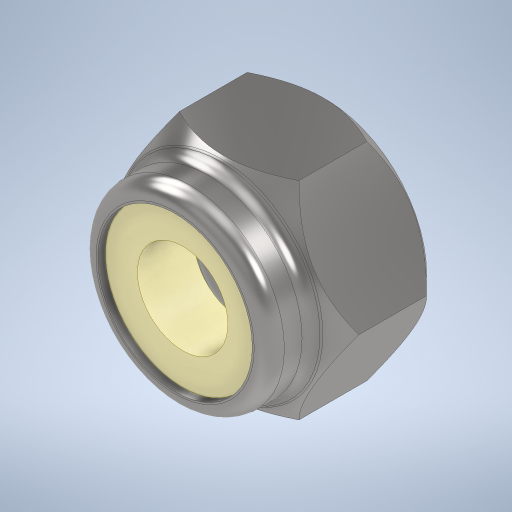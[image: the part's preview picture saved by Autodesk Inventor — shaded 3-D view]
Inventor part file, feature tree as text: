
AUTODESK INVENTOR PART (.ipt)
format: ipt  version: 2024 (Build 280153000, 153)  size: 372,224 bytes
history: native  units: mm
features: sketch x6, extrude x5, chamfer x2, hole x2, fillet x1, projected_geometry x1, other x1
ambient origin geometry x8: Origin, YZ Plane, XZ Plane, XY Plane, X Axis, Y Axis, Z Axis, Center Point
bodies: Solid1 (feature_tree)
feature tree (18):
  sketch  "Sketch1"  dims[d0=5.5mm d2=2.8mm d3=0.0mm d4=0.5mm d5=2.0mm d6=45.0deg]
  extrude  "Extrusion1"  Depth=2.8mm TaperAngle=0.0deg
  chamfer  "Chamfer1"  Distance=0.5mm Angle=45.0deg
  extrude  "Extrusion2"  Depth=5.0mm
  extrude  "Extrusion3"  Depth=0.4mm
  fillet  "Fillet1"  Radius=4.1mm
  extrude  "Extrusion4"  Depth=1.5mm TaperAngle=0.0deg
  extrude  "Extrusion5"  Depth=0.2mm TaperAngle=45.0deg
  hole  "Hole1"  [1 undecoded]
  hole  "Hole2"  [1 undecoded]
  chamfer  "Chamfer2"  [1 undecoded]
  sketch  "Sketch2"  dims[d7=0.0mm d8=0.0mm d9=5.0mm]
  sketch  "Sketch3"  dims[d10=1.2mm d11=0.0mm d12=0.4mm d13=4.1mm]
  sketch  "Sketch4"  dims[d14=1.7mm d15=0.0mm d16=1.5mm d17=0.0mm]
  projected_geometry  "Projected Loop1"
  other  "Lockring"
  sketch  "Sketch5"  dims[d18=2.459mm d19=6.0mm d20=4.0mm d21=2.0mm d22=90.0deg d23=11.8mm d24=0.0mm]
  sketch  "Sketch6"  dims[d25=2.4mm d26=8.0mm d27=4.0mm d28=2.0mm d29=90.0deg d30=8.0mm d31=0.0mm d32=0.2mm d33=2.0mm d34=45.0deg]
note: 3 required parameter values undecoded (feature->parameter linkage not recoverable at this tier; creation-order binding heuristic only, values carry confidence <= 0.55)
